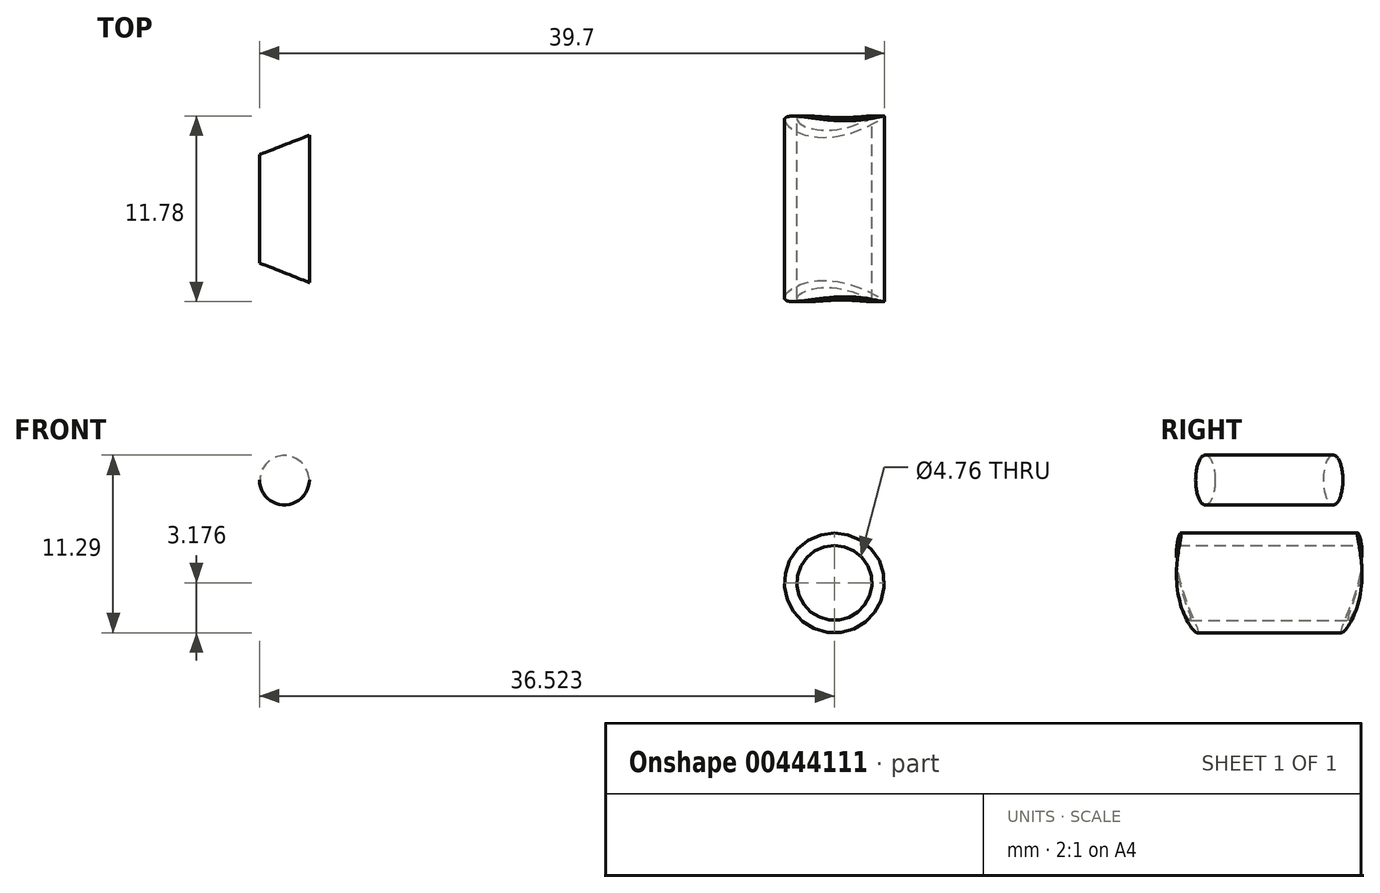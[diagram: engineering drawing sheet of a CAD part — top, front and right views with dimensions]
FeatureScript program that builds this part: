
annotation { "Feature Type Name" : "Feature", "Feature Type Description" : "" }
export const myFeature = defineFeature(function(context is Context, id is Id, definition is map)
    precondition{}
    {
        {
            var Q0;
            Q0=qCreatedBy(makeId("Front.planeOp"),FACE);
            var sketch = newSketch(context, id + "F0", { "sketchPlane" : qUnion([Q0])});
            skLineSegment(sketch, "E0", {"start": v(-1, 2.9) * mm, "end": v(0.18, 2.97) * mm});
            skPoint(sketch, "E1", {"position": v(48.62, 15.19) * mm});
            skPoint(sketch, "E2", {"position": v(13.69, 21.71) * mm});
            skArc(sketch, "E3", {"start": v(11.72, 27.52) * mm, "mid": v(7.86, 22.32) * mm, "end": v(11.07, 16.7) * mm});
            skFitSpline(sketch, "E4.trimOffspring", {"points": [v(-46.68, 0) * mm, v(-36.83, 14.74) * mm, v(0, 26.85) * mm, v(48.1, 23.51) * mm, v(54.92, 18.58) * mm, v(55.49, 12.52) * mm, v(51.4, 7.87) * mm, v(7.3, 16.37) * mm, v(0, 0) * mm], "startDerivative": vector(72.96, 165.42) * mm, "endDerivative": vector(-10.36, -190.7) * mm});
            skPoint(sketch, "E5.start.orphan", {"position": v(-1, 2.9) * mm});
            skPoint(sketch, "E6.start.orphan", {"position": v(-1.9, 17.09) * mm});
            skPoint(sketch, "E7.end.orphan", {"position": v(15.24, 75.7) * mm});
            skLineSegment(sketch, "E8", {"start": v(11.07, 16.7) * mm, "end": v(51.4, 7.87) * mm, "construction": true});
            skLineSegment(sketch, "E9", {"start": v(51.4, 7.87) * mm, "end": v(59.51, 44.88) * mm, "construction": true});
            skCircle(sketch, "E10", {"center": v(48.62, 15.19) * mm, "radius": 3.18 * mm});
            skCircle(sketch, "E11", {"center": v(13.69, 21.71) * mm, "radius": 1.59 * mm});
            skCircle(sketch, "E12", {"center": v(48.62, 15.19) * mm, "radius": 2.38 * mm});
            skSolve(sketch);
        }
        {
            var Q0;
            Q0=makeQuery(id+"F0.imprint","IMPRINT",FACE,{"disambiguationData":[TD([[makeQuery(id+"F0.imprint","IMPRINT",EDGE,{"derivedFrom":sQuery(id+"F0.wireOp",EDGE,"E10")}),1.0]])]});
            var Q1;
            Q1=makeQuery(id+"F0.imprint","IMPRINT",FACE,{"disambiguationData":[TD([[makeQuery(id+"F0.imprint","IMPRINT",EDGE,{"derivedFrom":sQuery(id+"F0.wireOp",EDGE,"E11")}),1.0]])]});
            extrude(context, id + "F1", {"entities" : qUnion([Q0, Q1]), "endBound" : BoundingType.SYMMETRIC, "depth" : 12.7 * mm, "offsetDistance" : 25.4 * mm});
        }
        {
            var Q0;
            Q0=sQuery(id+"F0.wireOp",EDGE,"E9");
            var Q1;
            Q1=qCreatedBy(makeId("Right.planeOp"),FACE);
            cPlane(context, id + "F2", {"entities" : qUnion([Q0, Q1]), "cplaneType" : CPlaneType.LINE_ANGLE, "offset" : 25.4 * mm, "angle" : 0 * degree, "width" : 152.4 * mm, "height" : 152.4 * mm});
        }
        {
            var Q0;
            Q0=qCreatedBy(id+"F2.planeOp",FACE);
            var sketch = newSketch(context, id + "F3", { "sketchPlane" : qUnion([Q0])});
            skLineSegment(sketch, "E13", {"start": v(0, 14.17) * mm, "end": v(0, 44.65) * mm});
            skLineSegment(sketch, "E14.bottom", {"start": v(-13.26, 16.68) * mm, "end": v(13.26, 16.68) * mm});
            skLineSegment(sketch, "E14.top", {"start": v(-13.26, 37.07) * mm, "end": v(13.26, 37.07) * mm});
            skLineSegment(sketch, "E14.left", {"start": v(-13.26, 16.68) * mm, "end": v(-13.26, 37.07) * mm});
            skLineSegment(sketch, "E14.right", {"start": v(13.26, 16.68) * mm, "end": v(13.26, 37.07) * mm});
            skPoint(sketch, "E14.middle", {"position": v(0, 26.87) * mm});
            skPoint(sketch, "E15", {"position": v(0, 9.1) * mm});
            skLineSegment(sketch, "E16", {"start": v(0, 14.17) * mm, "end": v(0, 9.1) * mm});
            skLineSegment(sketch, "E17.top", {"start": v(13.26, 10.15) * mm, "end": v(-13.26, 10.15) * mm});
            skLineSegment(sketch, "E17.left", {"start": v(13.26, 16.68) * mm, "end": v(13.26, 10.15) * mm});
            skLineSegment(sketch, "E17.right", {"start": v(-13.26, 16.68) * mm, "end": v(-13.26, 10.15) * mm});
            skFitSpline(sketch, "E18", {"points": [v(0, 34.75) * mm, v(4.18, 31.05) * mm, v(5.88, 26.87) * mm, v(4.57, 22.12) * mm, v(0, 17.61) * mm], "startDerivative": vector(18.03, -13.57) * mm, "endDerivative": vector(-19.34, -14.01) * mm});
            skFitSpline(sketch, "E19.MirrorCS", {"points": [v(0, 34.75) * mm, v(-4.18, 31.05) * mm, v(-5.88, 26.87) * mm, v(-4.57, 22.12) * mm, v(0, 17.61) * mm], "startDerivative": vector(-18.03, -13.57) * mm, "endDerivative": vector(19.34, -14.01) * mm});
            skSolve(sketch);
        }
        {
            var Q0;
            {var subQ0=sQuery(id+"F3.wireOp",EDGE,"E14.right");Q0=makeQuery(id+"F3.imprint","IMPRINT",FACE,{"disambiguationData":[TD([[makeQuery(id+"F3.imprint","IMPRINT",EDGE,{"derivedFrom":subQ0}),1.0]])]});}
            var Q1;
            {var subQ4=sQuery(id+"F3.wireOp",EDGE,"E14.left");Q1=makeQuery(id+"F3.imprint","IMPRINT",FACE,{"disambiguationData":[TD([[makeQuery(id+"F3.imprint","IMPRINT",EDGE,{"derivedFrom":subQ4}),-1.0]])]});}
            extrude(context, id + "F4", {"entities" : qUnion([Q0, Q1]), "operationType" : NewBodyOperationType.REMOVE, "endBound" : BoundingType.SYMMETRIC, "depth" : 127 * mm, "offsetDistance" : 25.4 * mm});
        }
        {
            var Q0;
            Q0=qCreatedBy(makeId("Top.planeOp"),FACE);
            var sketch = newSketch(context, id + "F5", { "sketchPlane" : qUnion([Q0])});
            skLineSegment(sketch, "E20", {"start": v(3.25, 0) * mm, "end": v(22.75, -7.58) * mm});
            skLineSegment(sketch, "E21", {"start": v(0, 0) * mm, "end": v(30.44, 0) * mm});
            skLineSegment(sketch, "E22.MirrorCS", {"start": v(3.25, 0) * mm, "end": v(22.75, 7.58) * mm});
            skLineSegment(sketch, "E23.bottom", {"start": v(0, -11.84) * mm, "end": v(16.71, -11.84) * mm});
            skLineSegment(sketch, "E23.top", {"start": v(0, 10.52) * mm, "end": v(16.71, 10.52) * mm});
            skLineSegment(sketch, "E23.left", {"start": v(0, -11.84) * mm, "end": v(0, 10.52) * mm});
            skLineSegment(sketch, "E24", {"start": v(16.71, 10.52) * mm, "end": v(21.9, 10.52) * mm});
            skLineSegment(sketch, "E25", {"start": v(21.9, 10.52) * mm, "end": v(22.39, -11.84) * mm});
            skLineSegment(sketch, "E26", {"start": v(22.39, -11.84) * mm, "end": v(16.71, -11.84) * mm});
            skSolve(sketch);
        }
        {
            var Q0;
            {var subQ0=sQuery(id+"F5.wireOp",EDGE,"E23.bottom");Q0=makeQuery(id+"F5.imprint","IMPRINT",FACE,{"disambiguationData":[TD([[makeQuery(id+"F5.imprint","IMPRINT",EDGE,{"derivedFrom":subQ0}),1.0]])]});}
            var Q1;
            {var subQ3=sQuery(id+"F5.wireOp",EDGE,"E23.top");Q1=makeQuery(id+"F5.imprint","IMPRINT",FACE,{"disambiguationData":[TD([[makeQuery(id+"F5.imprint","IMPRINT",EDGE,{"derivedFrom":subQ3}),-1.0]])]});}
            extrude(context, id + "F6", {"entities" : qUnion([Q0, Q1]), "operationType" : NewBodyOperationType.REMOVE, "endBound" : BoundingType.SYMMETRIC, "oppositeDirection" : true, "depth" : 76.2 * mm, "offsetDistance" : 25.4 * mm});
        }
    });
